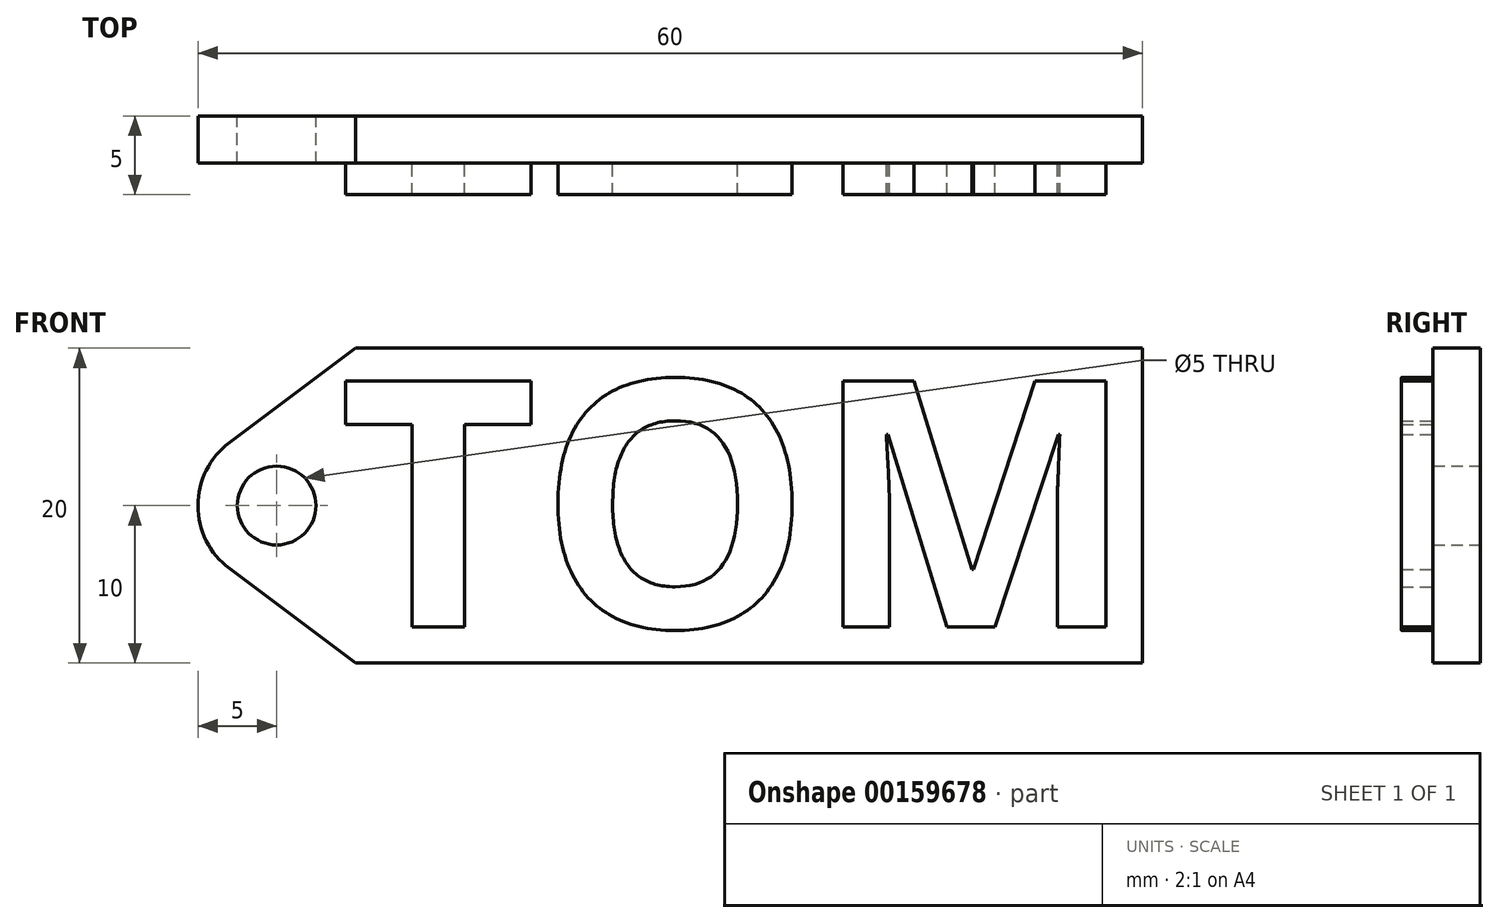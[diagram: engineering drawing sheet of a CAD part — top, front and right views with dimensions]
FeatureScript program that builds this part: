
annotation { "Feature Type Name" : "Feature", "Feature Type Description" : "" }
export const myFeature = defineFeature(function(context is Context, id is Id, definition is map)
    precondition{}
    {
        {
            var Q0;
            Q0=qCreatedBy(makeId("Front.planeOp"),FACE);
            var sketch = newSketch(context, id + "F0", { "sketchPlane" : qUnion([Q0])});
            skLineSegment(sketch, "E0.bottom", {"start": v(25, -10) * mm, "end": v(-25, -10) * mm});
            skLineSegment(sketch, "E0.top", {"start": v(25, 10) * mm, "end": v(-25, 10) * mm});
            skLineSegment(sketch, "E0.left", {"start": v(25, -10) * mm, "end": v(25, 10) * mm});
            skPoint(sketch, "E0.middle", {"position": v(0, 0) * mm});
            skCircle(sketch, "E1", {"center": v(-30, 0) * mm, "radius": 2.5 * mm});
            skLineSegment(sketch, "E2", {"start": v(-25, 10) * mm, "end": v(-33, 4) * mm});
            skArc(sketch, "E3", {"start": v(-33, 4) * mm, "mid": v(-34.47, 2.24) * mm, "end": v(-35, 0) * mm});
            skArc(sketch, "E4.MirrorCS", {"start": v(-33, -4) * mm, "mid": v(-34.47, -2.24) * mm, "end": v(-35, 0) * mm});
            skLineSegment(sketch, "E5.MirrorCS", {"start": v(-25, -10) * mm, "end": v(-33, -4) * mm});
            skSolve(sketch);
        }
        {
            var Q0;
            Q0=makeQuery(id+"F0.imprint","IMPRINT",FACE,{"disambiguationData":[TD([[makeQuery(id+"F0.imprint","IMPRINT",EDGE,{"derivedFrom":sQuery(id+"F0.wireOp",EDGE,"E0.bottom")}),-1.0]])]});
            extrude(context, id + "F1", {"entities" : qUnion([Q0]), "depth" : 3 * mm});
        }
        {
            var Q0;
            Q0=makeQuery(id+"F1.opExtrude","CAP_FACE",FACE,{"disambiguationData":[OSD([sQuery(id+"F0.wireOp",EDGE,"E0.bottom"),sQuery(id+"F0.wireOp",EDGE,"E0.top"),sQuery(id+"F0.wireOp",EDGE,"E0.left"),sQuery(id+"F0.wireOp",EDGE,"E1"),sQuery(id+"F0.wireOp",EDGE,"E2"),sQuery(id+"F0.wireOp",EDGE,"E3"),sQuery(id+"F0.wireOp",EDGE,"E4.MirrorCS"),sQuery(id+"F0.wireOp",EDGE,"E5.MirrorCS")])],"isStart":false});
            var sketch = newSketch(context, id + "F2", { "sketchPlane" : qUnion([Q0])});
            skText(sketch, "E6", { "text": "TOM\n", "fontName": "OpenSans-Bold.ttf"});
            const initialGuessF2  = {"E6": [-0.02607, -0.00772, 1, 0, 0.01575]};
            skSetInitialGuess(sketch, initialGuessF2);
            skSolve(sketch);
        }
        {
            var Q0;
            Q0=makeQuery(id+"F2.imprint","IMPRINT",FACE,{"disambiguationData":[TD([[makeQuery(id+"F2.imprint","IMPRINT",EDGE,{"derivedFrom":sQuery(id+"F2.wireOp",EDGE,"E6.sketch_text.stroke-0")}),-1.0]])]});
            var Q1;
            Q1=makeQuery(id+"F2.imprint","IMPRINT",FACE,{"disambiguationData":[TD([[makeQuery(id+"F2.imprint","IMPRINT",EDGE,{"derivedFrom":sQuery(id+"F2.wireOp",EDGE,"E6.sketch_text.stroke-8")}),-1.0]])]});
            var Q2;
            Q2=makeQuery(id+"F2.imprint","IMPRINT",FACE,{"disambiguationData":[TD([[makeQuery(id+"F2.imprint","IMPRINT",EDGE,{"derivedFrom":sQuery(id+"F2.wireOp",EDGE,"E6.sketch_text.stroke-22")}),-1.0]])]});
            extrude(context, id + "F3", {"entities" : qUnion([Q0, Q1, Q2]), "operationType" : NewBodyOperationType.ADD, "depth" : 2 * mm});
        }
    });
